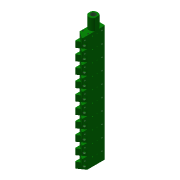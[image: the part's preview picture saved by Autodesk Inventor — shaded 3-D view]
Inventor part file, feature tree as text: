
AUTODESK INVENTOR PART (.ipt)
format: ipt  version: 2016 (Build 200138000, 138)  size: 688,128 bytes
history: native  units: mm
features: sketch x17, hole x12, extrude x6, other x6, plane x5, pattern_linear x2, reference x2, fillet x1, mirror x1, thread x1
ambient origin geometry x8: Origin, YZ Plane, XZ Plane, XY Plane, X Axis, Y Axis, Z Axis, Center Point
bodies: Volumenkörper1 (feature_tree), Volumenkörper2 (feature_tree), Volumenkörper3 (feature_tree)
feature tree (53):
  extrude  "Extrusion1"  Depth=40.0mm
  hole  "Bohrung1"  [1 undecoded]
  hole  "Bohrung2"  [1 undecoded]
  hole  "Bohrung3"  [1 undecoded]
  hole  "Bohrung4"  [1 undecoded]
  extrude  "Extrusion2"  Depth=8.5mm
  hole  "Bohrung5"  [1 undecoded]
  hole  "Bohrung6"  [1 undecoded]
  plane  "Arbeitsebene1"
  extrude  "Extrusion3"  Depth=5.5mm
  hole  "Bohrung7"  [1 undecoded]
  hole  "Bohrung8"  [1 undecoded]
  plane  "Arbeitsebene2"
  extrude  "Extrusion4"  Depth=8.0mm
  hole  "Bohrung9"  [1 undecoded]
  hole  "Bohrung10"  [1 undecoded]
  pattern_linear  "Rechteckige Anordnung3"  Spacing1=6.108652mm  [1 undecoded]
  hole  "Bohrung11"  [1 undecoded]
  plane  "Arbeitsebene3"
  extrude  "Extrusion6"  [1 undecoded]
  fillet  "Rundung1"  Radius=6.108652mm
  hole  "Bohrung13"  [1 undecoded]
  plane  "Arbeitsebene6"
  other  "Trennen2"
  pattern_linear  "Rechteckige Anordnung4"  Count1=5  [1 undecoded]
  plane  "Arbeitsebene4"
  mirror  "Spiegeln2"
  extrude  "Extrusion10"  TaperAngle=90.0deg  [1 undecoded]
  other  "Kombinieren1"
  thread  "Gewinde3"  [1 undecoded]
  sketch  "Skizze1"  dims[d0=13.0mm d1=40.0mm]
  sketch  "Skizze2"  dims[d2=60.0mm d3=0.0mm d4=29.5mm]
  sketch  "Skizze3"  dims[d5=5.25mm d6=5.0mm]
  sketch  "Skizze4"  dims[d7=5.0mm]
  sketch  "Skizze5"  dims[d8=2.459mm d9=4.0mm d10=4.0mm d11=2.0mm d12=90.0deg d13=5.0mm d14=20.594885mm d15=5.25mm]
  sketch  "Skizze6"  dims[d16=29.5mm d17=15.0mm]
  sketch  "Skizze7"  dims[d18=15.0mm]
  sketch  "Skizze8"  dims[d19=2.459mm d20=4.0mm d21=4.0mm d22=2.0mm d23=90.0deg d24=5.0mm d25=20.594885mm d26=8.5mm]
  sketch  "Skizze9"  dims[d27=1.2mm d28=4.0mm d29=4.0mm d30=2.0mm d31=90.0deg d32=5.0mm d33=20.594885mm d35=8.5mm]
  sketch  "Skizze10"  dims[d36=15.0mm]
  sketch  "Skizze11"  dims[d37=1.2mm d38=4.0mm d39=4.0mm d40=2.0mm d41=90.0deg d42=5.0mm d43=20.594885mm d44=8.0mm]
  sketch  "Skizze12"  dims[d45=6.5mm d46=5.5mm]
  sketch  "Skizze13"  dims[d48=0.6mm d49=105.0mm d50=0.0mm]
  sketch  "Skizze14"  dims[d57=8.0mm d58=5.0mm]
  sketch  "Skizze15"  dims[d59=1.8mm d60=6.0mm d61=4.0mm d62=2.0mm d63=90.0deg d64=2.0mm d65=20.594885mm d66=8.0mm]
  other  "Arbeitsachse1"
  sketch  "Skizze18"  dims[d67=15.0mm]
  sketch  "Skizze19"  dims[d68=1.8mm d69=6.0mm d70=4.0mm d71=2.0mm d72=90.0deg d73=2.0mm d74=20.594885mm d75=-5.0mm d76=1.8mm d77=6.108652mm d78=10.0mm d79=0.0mm d80=1.8mm d81=6.0mm d82=4.0mm d83=2.0mm d84=90.0deg d85=14.3mm d86=20.594885mm d87=4.134mm d88=3.0mm d89=4.0mm d90=2.0mm d91=90.0deg d92=4.0mm d93=20.594885mm d94=-15.0mm d95=6.108652mm d96=10.0mm d97=0.0mm d98=1.8mm d99=3.0mm d100=4.0mm d101=2.0mm d102=90.0deg d103=14.3mm d104=20.594885mm d105=4.134mm d106=3.0mm d107=4.0mm d108=2.0mm d109=90.0deg d110=4.0mm d111=20.594885mm d112=50.0mm d114=20.0mm d115=8.566mm d116=3.0mm d117=4.0mm d118=2.0mm d119=90.0deg d120=10.0mm d121=20.594885mm d122=90.0deg d137=15.0mm d138=20.0mm d139=0.0mm d140=1.0mm d141=2.459mm d142=6.0mm d143=4.0mm d144=2.0mm d145=90.0deg d146=8.0mm d147=20.594885mm d171=-100.0mm d173=8.8mm d174=8.0mm d175=0.0mm d178=0.0mm d179=90.0mm d181=20.0mm d182=10.0mm d183=0.0mm]
  reference  "Referenz1"
  reference  "Referenz2"
  other  "Schnittkanten projizieren1"
  other  "Schnittkanten projizieren2"
  other  "Schnittkanten projizieren3"
note: 17 required parameter values undecoded (feature->parameter linkage not recoverable at this tier; creation-order binding heuristic only, values carry confidence <= 0.55)
